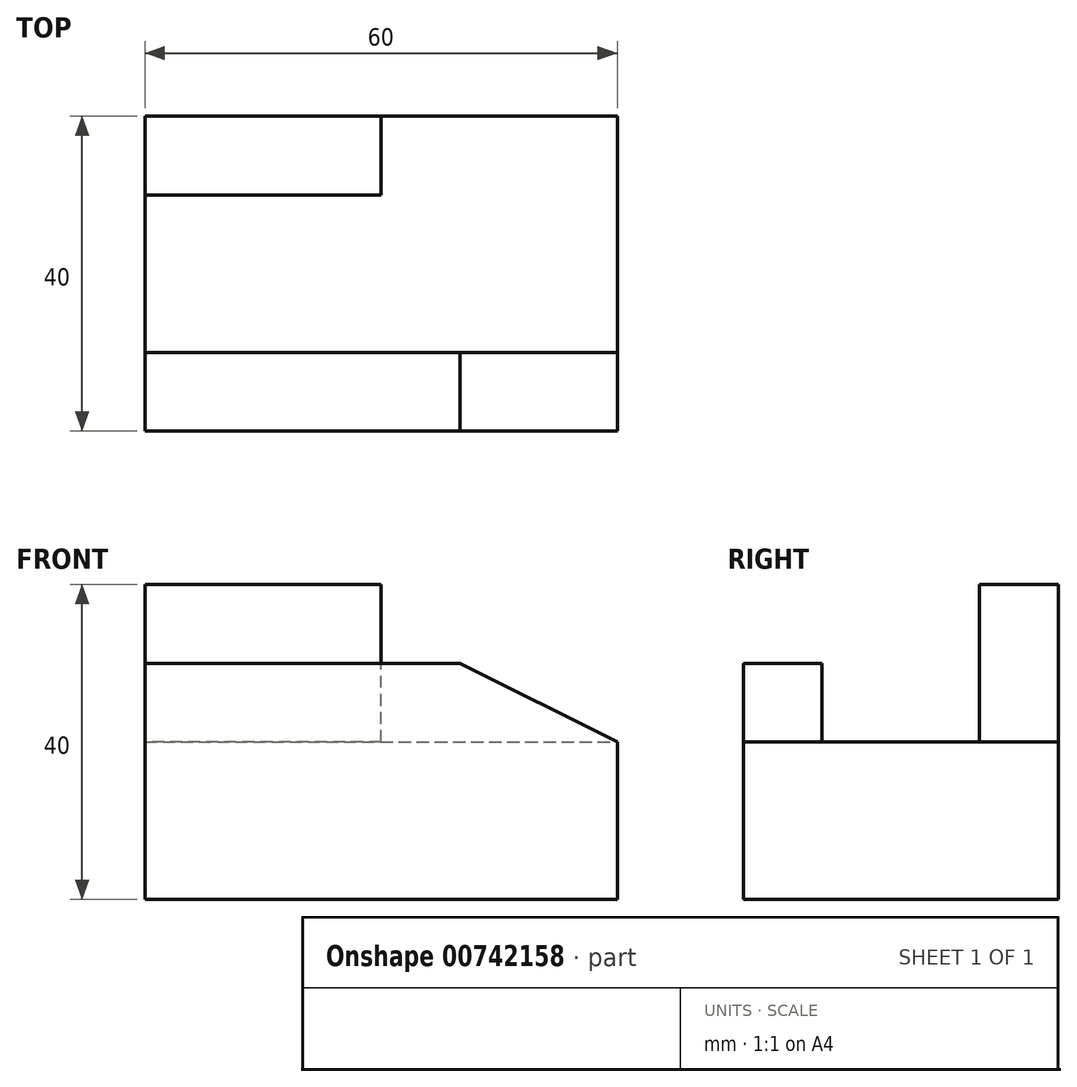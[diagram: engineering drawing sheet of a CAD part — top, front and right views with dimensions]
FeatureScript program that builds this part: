
annotation { "Feature Type Name" : "Feature", "Feature Type Description" : "" }
export const myFeature = defineFeature(function(context is Context, id is Id, definition is map)
    precondition{}
    {
        {
            var Q0;
            Q0=qCreatedBy(makeId("Top.planeOp"),FACE);
            var sketch = newSketch(context, id + "F0", { "sketchPlane" : qUnion([Q0])});
            skLineSegment(sketch, "E0", {"start": v(0, 0) * mm, "end": v(60, 0) * mm});
            skLineSegment(sketch, "E1", {"start": v(60, 0) * mm, "end": v(60, 40) * mm});
            skLineSegment(sketch, "E2", {"start": v(0, 0) * mm, "end": v(0, 40) * mm});
            skLineSegment(sketch, "E3", {"start": v(0, 40) * mm, "end": v(60, 40) * mm});
            skSolve(sketch);
        }
        {
            var Q0;
            Q0=makeQuery(id+"F0.imprint","IMPRINT",FACE,{"disambiguationData":[TD([[makeQuery(id+"F0.imprint","IMPRINT",EDGE,{"derivedFrom":sQuery(id+"F0.wireOp",EDGE,"E0")}),1.0]])]});
            extrude(context, id + "F1", {"entities" : qUnion([Q0]), "depth" : 40 * mm, "offsetDistance" : 25 * mm});
        }
        {
            var Q0;
            Q0=makeQuery(id+"F1.opExtrude","CAP_FACE",FACE,{"disambiguationData":[OSD([sQuery(id+"F0.wireOp",EDGE,"E0"),sQuery(id+"F0.wireOp",EDGE,"E1"),sQuery(id+"F0.wireOp",EDGE,"E2"),sQuery(id+"F0.wireOp",EDGE,"E3")])],"isStart":false});
            var sketch = newSketch(context, id + "F2", { "sketchPlane" : qUnion([Q0])});
            skLineSegment(sketch, "E4", {"start": v(0, 40) * mm, "end": v(30, 40) * mm});
            skLineSegment(sketch, "E5", {"start": v(30, 40) * mm, "end": v(30, 30) * mm});
            skLineSegment(sketch, "E6", {"start": v(30, 30) * mm, "end": v(0, 30) * mm});
            skSolve(sketch);
        }
        {
            var Q0;
            {var subQ3=sQuery(id+"F2.wireOp",EDGE,"E5");Q0=makeQuery(id+"F2.imprint","IMPRINT",FACE,{"disambiguationData":[TD([[makeQuery(id+"F2.imprint","IMPRINT",EDGE,{"derivedFrom":subQ3}),1.0]])]});}
            var sketch = newSketch(context, id + "F3", { "sketchPlane" : qUnion([Q0])});
            skLineSegment(sketch, "E7", {"start": v(60, 0) * mm, "end": v(60, 10) * mm});
            skLineSegment(sketch, "E8", {"start": v(60, 10) * mm, "end": v(0, 10) * mm});
            skLineSegment(sketch, "E9", {"start": v(0, 10) * mm, "end": v(0, 0) * mm});
            skSolve(sketch);
        }
        {
            var Q0;
            {var subQ3=sQuery(id+"F2.wireOp",EDGE,"E5");Q0=makeQuery(id+"F2.imprint","IMPRINT",FACE,{"disambiguationData":[TD([[makeQuery(id+"F2.imprint","IMPRINT",EDGE,{"derivedFrom":subQ3}),1.0]])]});}
            extrude(context, id + "F4", {"entities" : qUnion([Q0]), "operationType" : NewBodyOperationType.REMOVE, "oppositeDirection" : true, "depth" : 20 * mm, "offsetDistance" : 25 * mm});
        }
        {
            var Q0;
            Q0=makeQuery(id+"F3.imprint","IMPRINT",FACE,{"disambiguationData":[TD([[makeQuery(id+"F3.imprint","IMPRINT",EDGE,{"derivedFrom":sQuery(id+"F3.wireOp",EDGE,"E7")}),1.0]])]});
            extrude(context, id + "F5", {"entities" : qUnion([Q0]), "operationType" : NewBodyOperationType.REMOVE, "depth" : 10 * mm, "offsetDistance" : 25 * mm});
        }
        {
            var Q0;
            Q0=makeQuery(id+"F4.boolean.opBoolean","COPY",FACE,{"derivedFrom":makeQuery(id+"F4.opExtrude","CAP_FACE",FACE,{"disambiguationData":[OSD([sQuery(id+"F0.wireOp",EDGE,"E0"),sQuery(id+"F0.wireOp",EDGE,"E1"),sQuery(id+"F0.wireOp",EDGE,"E2"),sQuery(id+"F0.wireOp",EDGE,"E3"),sQuery(id+"F2.wireOp",EDGE,"E5"),sQuery(id+"F2.wireOp",EDGE,"E6")])],"isStart":false})});
            var sketch = newSketch(context, id + "F6", { "sketchPlane" : qUnion([Q0])});
            skLineSegment(sketch, "E10", {"start": v(0, 0) * mm, "end": v(0, 10) * mm});
            skLineSegment(sketch, "E11", {"start": v(0, 10) * mm, "end": v(60, 10) * mm});
            skLineSegment(sketch, "E12", {"start": v(60, 10) * mm, "end": v(60, 0) * mm});
            skLineSegment(sketch, "E13", {"start": v(60, 0) * mm, "end": v(0, 0) * mm});
            skSolve(sketch);
        }
        {
            var Q0;
            Q0=makeQuery(id+"F6.imprint","IMPRINT",FACE,{"disambiguationData":[TD([[makeQuery(id+"F6.imprint","IMPRINT",EDGE,{"derivedFrom":sQuery(id+"F6.wireOp",EDGE,"E10")}),-1.0]])]});
            extrude(context, id + "F7", {"entities" : qUnion([Q0]), "operationType" : NewBodyOperationType.ADD, "depth" : 10 * mm, "offsetDistance" : 25 * mm});
        }
        {
            var Q0;
            Q0=makeQuery(id+"F7.opExtrude","CAP_FACE",FACE,{"disambiguationData":[OSD([sQuery(id+"F6.wireOp",EDGE,"E10"),sQuery(id+"F6.wireOp",EDGE,"E11"),sQuery(id+"F6.wireOp",EDGE,"E12"),sQuery(id+"F6.wireOp",EDGE,"E13")])],"isStart":false});
            var sketch = newSketch(context, id + "F8", { "sketchPlane" : qUnion([Q0])});
            skLineSegment(sketch, "E14", {"start": v(60, 0) * mm, "end": v(40, 0) * mm});
            skLineSegment(sketch, "E15", {"start": v(40, 0) * mm, "end": v(40, 10) * mm});
            skLineSegment(sketch, "E16", {"start": v(40, 10) * mm, "end": v(60, 10) * mm});
            skLineSegment(sketch, "E17", {"start": v(60, 10) * mm, "end": v(60, 0) * mm});
            skSolve(sketch);
        }
        {
            var Q0;
            Q0=makeQuery(id+"F8.imprint","IMPRINT",FACE,{"disambiguationData":[TD([[makeQuery(id+"F8.imprint","IMPRINT",EDGE,{"derivedFrom":sQuery(id+"F8.wireOp",EDGE,"E14")}),1.0]])]});
            extrude(context, id + "F9", {"entities" : qUnion([Q0]), "operationType" : NewBodyOperationType.REMOVE, "oppositeDirection" : true, "depth" : 10 * mm, "offsetDistance" : 25 * mm});
        }
        {
            var Q0;
            Q0=makeQuery(id+"F7.boolean.opBoolean","MERGE",FACE,{"derivedFrom":[makeQuery(id+"F1.opExtrude","SWEPT_FACE",FACE,{"disambiguationData":[OSD([sQuery(id+"F0.wireOp",EDGE,"E0")])]}),makeQuery(id+"F7.opExtrude","SWEPT_FACE",FACE,{"disambiguationData":[OSD([sQuery(id+"F6.wireOp",EDGE,"E13")])]})]});
            var sketch = newSketch(context, id + "F10", { "sketchPlane" : qUnion([Q0])});
            skLineSegment(sketch, "E18", {"start": v(40, 30) * mm, "end": v(60, 20) * mm});
            skSolve(sketch);
        }
        {
            var Q0;
            Q0=makeQuery(id+"F10.imprint","IMPRINT",FACE,{"disambiguationData":[TD([[makeQuery(id+"F10.imprint","IMPRINT",EDGE,{"derivedFrom":sQuery(id+"F10.wireOp",EDGE,"E18")}),-1.0]])]});
            extrude(context, id + "F11", {"entities" : qUnion([Q0]), "operationType" : NewBodyOperationType.ADD, "oppositeDirection" : true, "depth" : 10 * mm, "offsetDistance" : 25 * mm});
        }
    });
